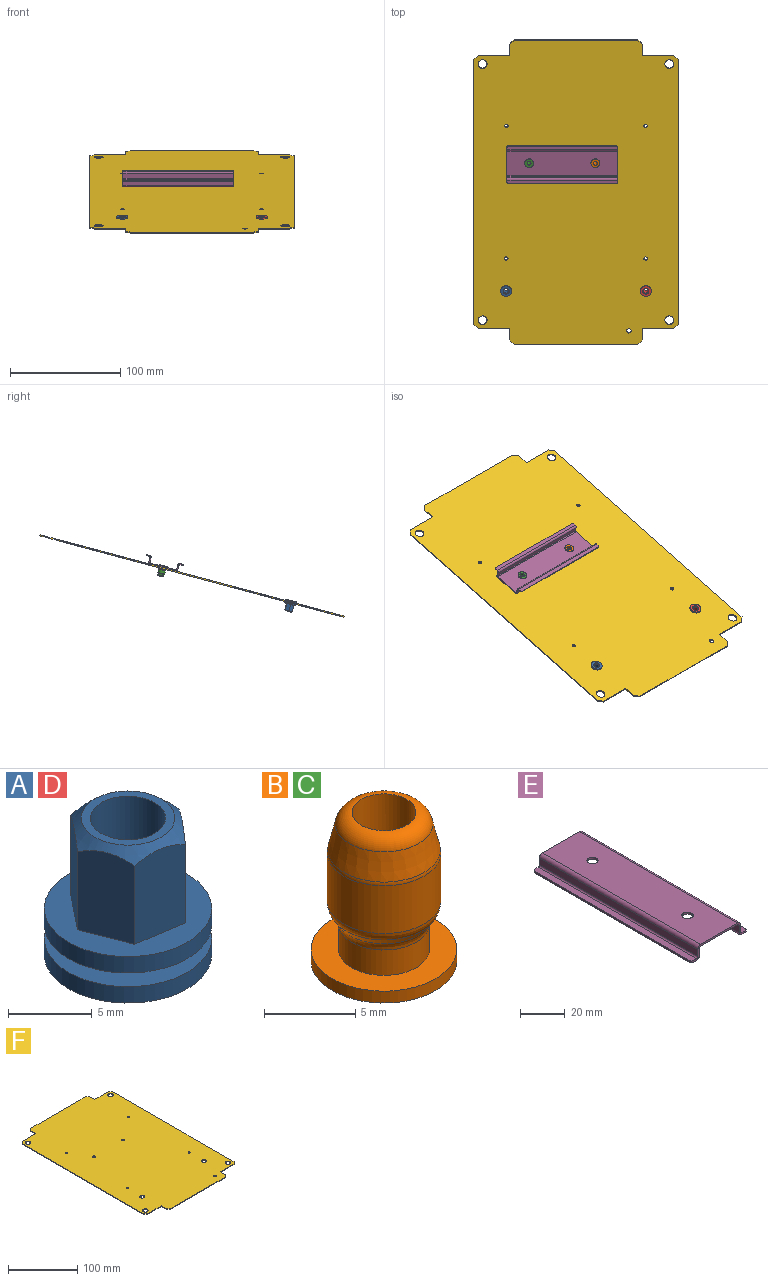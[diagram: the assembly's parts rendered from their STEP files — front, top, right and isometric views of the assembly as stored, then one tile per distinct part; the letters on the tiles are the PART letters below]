
ASSEMBLY  parts=6 mates=5
PART A: 18 faces, bbox 10x10x10 mm
  f0: plane 5.6x5.6mm, normal (0,0,1), area 8.7mm2, adj f1,f9
  f1: cone r=2.8mm half-angle=47.1deg, axis (0,0,-1), area 16.3mm2, adj f0,f12,f13,f14,f15,f16,f17
  f2: plane 10x10mm, normal (0,0,1), area 42mm2, adj f3,f12,f13,f14,f15,f16,f17
  f3: cylinder r=5mm len=10mm, axis (0,0,-1), area 37.7mm2, adj f2,f4
  f4: plane 10x10mm, normal (0,0,-1), area 40.1mm2, adj f3,f5
  f5: cylinder r=3.5mm len=7mm, axis (0,0,-1), area 22mm2, adj f4,f6
  f6: plane 10x10mm, normal (0,0,1), area 40.1mm2, adj f5,f7
  f7: cylinder r=5mm len=10mm, axis (0,0,-1), area 37.7mm2, adj f6,f8
  f8: plane 10x10mm, normal (0,0,-1), area 54.8mm2, adj f7,f11
  f9: cylinder r=2.25mm len=8.8mm, axis (0,0,1), area 124.4mm2, adj f0,f10
  f10: plane 5.5x5.5mm, normal (0,0,-1), area 7.9mm2, adj f9,f11
  f11: cylinder r=2.75mm len=5.5mm, axis (0,0,-1), area 20.7mm2, adj f8,f10
  f12: plane 6.19x3.71mm, normal (-0.15,-0.99,0), area 22.6mm2, adj f1,f2,f16,f17
  f13: plane 6.19x3.49mm, normal (0.93,0.36,0), area 22.6mm2, adj f1,f2,f15,f16
  f14: plane 6.19x2.93mm, normal (-0.78,0.62,0), area 22.6mm2, adj f1,f2,f15,f17
  f15: plane 6.19x3.71mm, normal (0.15,0.99,0), area 22.6mm2, adj f1,f2,f13,f14
  f16: plane 6.19x2.93mm, normal (0.78,-0.62,0), area 22.6mm2, adj f1,f2,f12,f13
  f17: plane 6.22x3.53mm, normal (-0.93,-0.36,0), area 22.6mm2, adj f1,f2,f12,f14
PART B: 12 faces, bbox 8x8x10 mm
  f0: plane 8x8mm, normal (0,0,-1), area 40.6mm2, adj f6,f7
  f1: cone r=2.5mm half-angle=13.2deg, axis (0,0,-1), area 32.4mm2, adj f8,f9
  f2: cylinder r=3.12mm len=6.24mm, axis (0,0,-1), area 62.9mm2, adj f9,f10
  f3: cone r=2.5mm half-angle=33deg, axis (0,0,1), area 9.6mm2, adj f10,f11
  f4: cylinder r=2.5mm len=5mm, axis (0,0,-1), area 26.8mm2, adj f5,f11
  f5: plane 8x8mm, normal (0,0,1), area 30.6mm2, adj f4,f6
  f6: cylinder r=4mm len=8mm, axis (0,0,-1), area 20.1mm2, adj f0,f5
  f7: cylinder r=1.75mm len=10mm, axis (0,0,1), area 110mm2, adj f0,f8
  f8: torus R=1.71mm, axis (0,0,1), area 18.8mm2, adj f1,f7
  f9: torus R=2.12mm, axis (0,0,1), area 4.5mm2, adj f1,f2
  f10: torus R=2.12mm, axis (0,0,1), area 11.1mm2, adj f2,f3
  f11: torus R=3.5mm, axis (0,0,-1), area 9.2mm2, adj f3,f4
PART C: same geometry as B
PART D: same geometry as A
PART E: 28 faces, bbox 35x100x7.5 mm
  f0: plane 100x3.2mm, normal (0,0,1), area 319.6mm2, adj f1,f19,f20,f21,f25,f27
  f1: cylinder r=0.8mm len=100mm, axis (0,1,0), area 125.7mm2, adj f0,f2,f20,f21
  f2: plane 100x3.9mm, normal (1,0,0), area 390mm2, adj f1,f3,f20,f21
  f3: cylinder r=1.8mm len=100mm, axis (0,1,0), area 282.7mm2, adj f2,f4,f20,f21
  f4: plane 100x23.4mm, normal (0,0,1), area 2300.7mm2, adj f3,f5,f20,f21,f22,f23
  f5: cylinder r=1.8mm len=100mm, axis (0,1,0), area 282.7mm2, adj f4,f6,f20,f21
  f6: plane 100x3.9mm, normal (-1,0,0), area 390mm2, adj f5,f7,f20,f21
  f7: cylinder r=0.8mm len=100mm, axis (0,1,0), area 125.7mm2, adj f6,f8,f20,f21
  f8: plane 100x3.2mm, normal (0,0,1), area 319.6mm2, adj f7,f9,f20,f21,f24,f26
  f9: plane 98x1mm, normal (-1,0,0), area 98mm2, adj f8,f10,f24,f26
  f10: plane 100x3.2mm, normal (0,0,-1), area 319.6mm2, adj f9,f11,f20,f21,f24,f26
  f11: cylinder r=1.8mm len=100mm, axis (0,1,0), area 282.7mm2, adj f10,f12,f20,f21
  f12: plane 100x3.9mm, normal (1,0,0), area 390mm2, adj f11,f13,f20,f21
  f13: cylinder r=0.8mm len=100mm, axis (0,1,0), area 125.7mm2, adj f12,f14,f20,f21
  f14: plane 100x23.4mm, normal (0,0,-1), area 2300.7mm2, adj f13,f15,f20,f21,f22,f23
  f15: cylinder r=0.8mm len=100mm, axis (0,1,0), area 125.7mm2, adj f14,f16,f20,f21
  f16: plane 100x3.9mm, normal (-1,0,0), area 390mm2, adj f15,f17,f20,f21
  f17: cylinder r=1.8mm len=100mm, axis (0,1,0), area 282.7mm2, adj f16,f18,f20,f21
  f18: plane 100x3.2mm, normal (0,0,-1), area 319.6mm2, adj f17,f19,f20,f21,f25,f27
  f19: plane 98x1mm, normal (1,0,0), area 98mm2, adj f0,f18,f25,f27
  f20: plane 33x7.5mm, normal (0,-1,0), area 43.8mm2, adj f0,f1,f2,f3,f4,f5,f6,f7
  f21: plane 33x7.5mm, normal (0,1,0), area 43.8mm2, adj f0,f1,f2,f3,f4,f5,f6,f7
  f22: cylinder r=2.5mm len=5mm, axis (0,0,1), area 15.7mm2, adj f4,f14
  f23: cylinder r=2.5mm len=5mm, axis (0,0,1), area 15.7mm2, adj f4,f14
  f24: cylinder r=1mm len=1mm, axis (0,0,-1), area 1.6mm2, adj f8,f9,f10,f21
  f25: cylinder r=1mm len=1mm, axis (0,0,1), area 1.6mm2, adj f0,f18,f19,f21
  f26: cylinder r=1mm len=1mm, axis (0,0,1), area 1.6mm2, adj f8,f9,f10,f20
  f27: cylinder r=1mm len=1mm, axis (0,0,-1), area 1.6mm2, adj f0,f18,f19,f20
PART F: 35 faces, bbox 185x285x1 mm
  f0: plane 248.4x1mm, normal (-1,0,0), area 248.4mm2, adj f25,f26,f27,f34
  f1: plane 28.5x1mm, normal (0,-1,0), area 28.5mm2, adj f2,f25,f26,f27
  f2: plane 10.3x1mm, normal (-1,0,0), area 10.3mm2, adj f1,f25,f26,f28
  f3: plane 112x1mm, normal (0,-1,0), area 112mm2, adj f25,f26,f28,f29
  f4: plane 10.3x1mm, normal (1,0,0), area 10.3mm2, adj f5,f25,f26,f29
  f5: plane 28.5x1mm, normal (0,-1,0), area 28.5mm2, adj f4,f25,f26,f30
  f6: plane 248.4x1mm, normal (1,0,0), area 248.4mm2, adj f25,f26,f30,f31
  f7: plane 28.5x1mm, normal (0,1,0), area 28.5mm2, adj f8,f25,f26,f31
  f8: plane 10.3x1mm, normal (1,0,0), area 10.3mm2, adj f7,f25,f26,f32
  f9: plane 112x1mm, normal (0,1,0), area 112mm2, adj f25,f26,f32,f33
  f10: plane 10.3x1mm, normal (-1,0,0), area 10.3mm2, adj f24,f25,f26,f33
  f11: cylinder r=4mm len=8mm, axis (0,0,-1), area 25.1mm2, adj f25,f26
  f12: cylinder r=4mm len=8mm, axis (0,0,-1), area 25.1mm2, adj f25,f26
  f13: cylinder r=2mm len=4mm, axis (0,0,-1), area 12.6mm2, adj f25,f26
  f14: cylinder r=1.5mm len=3mm, axis (0,0,-1), area 9.4mm2, adj f25,f26
  f15: cylinder r=1.5mm len=3mm, axis (0,0,-1), area 9.4mm2, adj f25,f26
  f16: cylinder r=1.5mm len=3mm, axis (0,0,-1), area 9.4mm2, adj f25,f26
  f17: cylinder r=2.5mm len=5mm, axis (0,0,-1), area 15.7mm2, adj f25,f26
  f18: cylinder r=2.5mm len=5mm, axis (0,0,-1), area 15.7mm2, adj f25,f26
  f19: cylinder r=3.5mm len=7mm, axis (0,0,-1), area 22mm2, adj f25,f26
  f20: cylinder r=3.5mm len=7mm, axis (0,0,-1), area 22mm2, adj f25,f26
  f21: cylinder r=1.5mm len=3mm, axis (0,0,-1), area 9.4mm2, adj f25,f26
  f22: cylinder r=4mm len=8mm, axis (0,0,-1), area 25.1mm2, adj f25,f26
  f23: cylinder r=4mm len=8mm, axis (0,0,-1), area 25.1mm2, adj f25,f26
  f24: plane 28.5x1mm, normal (0,1,0), area 28.5mm2, adj f10,f25,f26,f34
  f25: plane 285x185mm, normal (0,0,1), area 50443.9mm2, adj f0,f1,f2,f3,f4,f5,f6,f7
  f26: plane 285x185mm, normal (0,0,-1), area 50443.9mm2, adj f0,f1,f2,f3,f4,f5,f6,f7
  f27: plane 4x4mm, normal (-0.71,-0.71,0), area 5.7mm2, adj f0,f1,f25,f26
  f28: plane 4x4mm, normal (-0.71,-0.71,0), area 5.7mm2, adj f2,f3,f25,f26
  f29: plane 4x4mm, normal (0.71,-0.71,0), area 5.7mm2, adj f3,f4,f25,f26
  f30: plane 4x4mm, normal (0.71,-0.71,0), area 5.7mm2, adj f5,f6,f25,f26
  f31: plane 4x4mm, normal (0.71,0.71,0), area 5.7mm2, adj f6,f7,f25,f26
  f32: plane 4x4mm, normal (0.71,0.71,0), area 5.7mm2, adj f8,f9,f25,f26
  f33: plane 4x4mm, normal (-0.71,0.71,0), area 5.7mm2, adj f9,f10,f25,f26
  f34: plane 4x4mm, normal (-0.71,0.71,0), area 5.7mm2, adj f0,f24,f25,f26
PLACE A rot(axis=(0,0.99,0.13),180deg) t=(10.12,45.66,-195.4)mm
PLACE B rot(axis=(-1,0,0),165deg) t=(90.87,161.41,-163.77)mm
PLACE C rot(axis=(-1,0,0),165deg) t=(30.87,161.41,-163.77)mm
PLACE D rot(axis=(-1,0,0),165deg) t=(136.62,45.66,-195.4)mm
PLACE E rot(axis=(-0.7,-0.7,-0.09),169.4deg) t=(60.87,159.94,-158.26)mm
PLACE F rot(axis=(1,0,0),15deg) t=(73.37,135.44,-173.11)mm
MATE fastened C.f1 <-> E.f22  axis (0,0.26,-0.97) through (30.87,161.62,-164.54)mm
MATE fastened A.f1 <-> F.f19  axis (0,-0.26,0.97) through (10.12,46.22,-197.53)mm
MATE fastened F.f17 <-> E.f22  axis (0,-0.26,0.97) through (30.87,161.88,-165.51)mm
MATE fastened B.f1 <-> E.f23  axis (0,0.26,-0.97) through (90.87,161.62,-164.54)mm
MATE fastened F.f20 <-> D.f1  axis (0,0.26,-0.97) through (136.62,46.22,-197.53)mm
